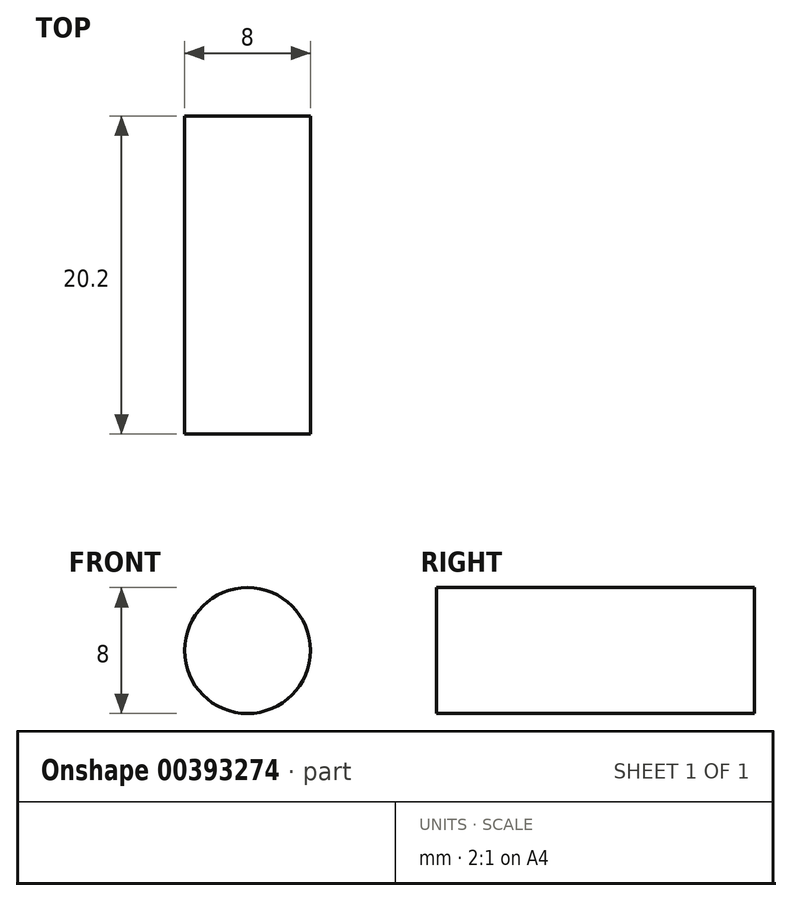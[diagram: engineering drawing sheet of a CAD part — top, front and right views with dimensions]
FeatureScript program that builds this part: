
annotation { "Feature Type Name" : "Feature", "Feature Type Description" : "" }
export const myFeature = defineFeature(function(context is Context, id is Id, definition is map)
    precondition{}
    {
        {
            var Q0;
            Q0=qCreatedBy(makeId("Front.planeOp"),FACE);
            var sketch = newSketch(context, id + "F0", { "sketchPlane" : qUnion([Q0])});
            skCircle(sketch, "E0", {"center": v(0, 0) * mm, "radius": 4 * mm});
            skSolve(sketch);
        }
        {
            var Q0;
            Q0 = qSketchRegion(id + "F0", true);
            extrude(context, id + "F1", {"entities" : qUnion([Q0]), "oppositeDirection" : true, "depth" : 20.2 * mm});
        }
    });
